# Revit family: QP01542154
name_source: partatom
category: Apparecchi idraulici
units: mm (PartAtom-declared; Revit-internal decimal feet)

## family parameters
Basato su piano di lavoro = No
Condiviso = No
Numero OmniClass = 23.45.00.00
Punto di calcolo locali = No
Quota connettore circolare = Usa diametro
Sempre verticale = Sì
Taglio con vuoti quando caricato = No
Tipo di parte = Normale
Titolo OmniClass = Sanitary, Laundry, and Cleaning Equipment

## types (1)
- QP01542154
    Commenti sul tipo = Realizzato in ottemperanza ai requisiti gestionali della norma EN ISO 9001.
Collaudato al 100% secondo la normativa EN 12266-1
    Descrizione = Utilizzato nell’impiantistica distributiva di gas a bassa pressione per le categorie:
Gas naturali: gas derivati dal petrolio (Metano) e gas di ricambio.
Gas di città: prodotti secondo i diversi procedimenti (Cracking - Cokerie - ecc.).
Gas liquidi: propano e miscele di gas propano/butano
    Materiale = Prodotto in lega di ottone conforme alla norma EN 12165-CW617N-DW
    Modello = Cim 112G
    Pressione nominale = MOP 5
    Produttore = CIMBERIO SPA
    Prospetto di default = 0 mm  [stored 0 ft]
    Temperatura di esercizio = -20 ÷ 60°C
    URL = https://web.cimberio.com

note: [stored X ft] marks values corroborated as IEEE doubles in the binary element streams (Revit-internal decimal feet)
